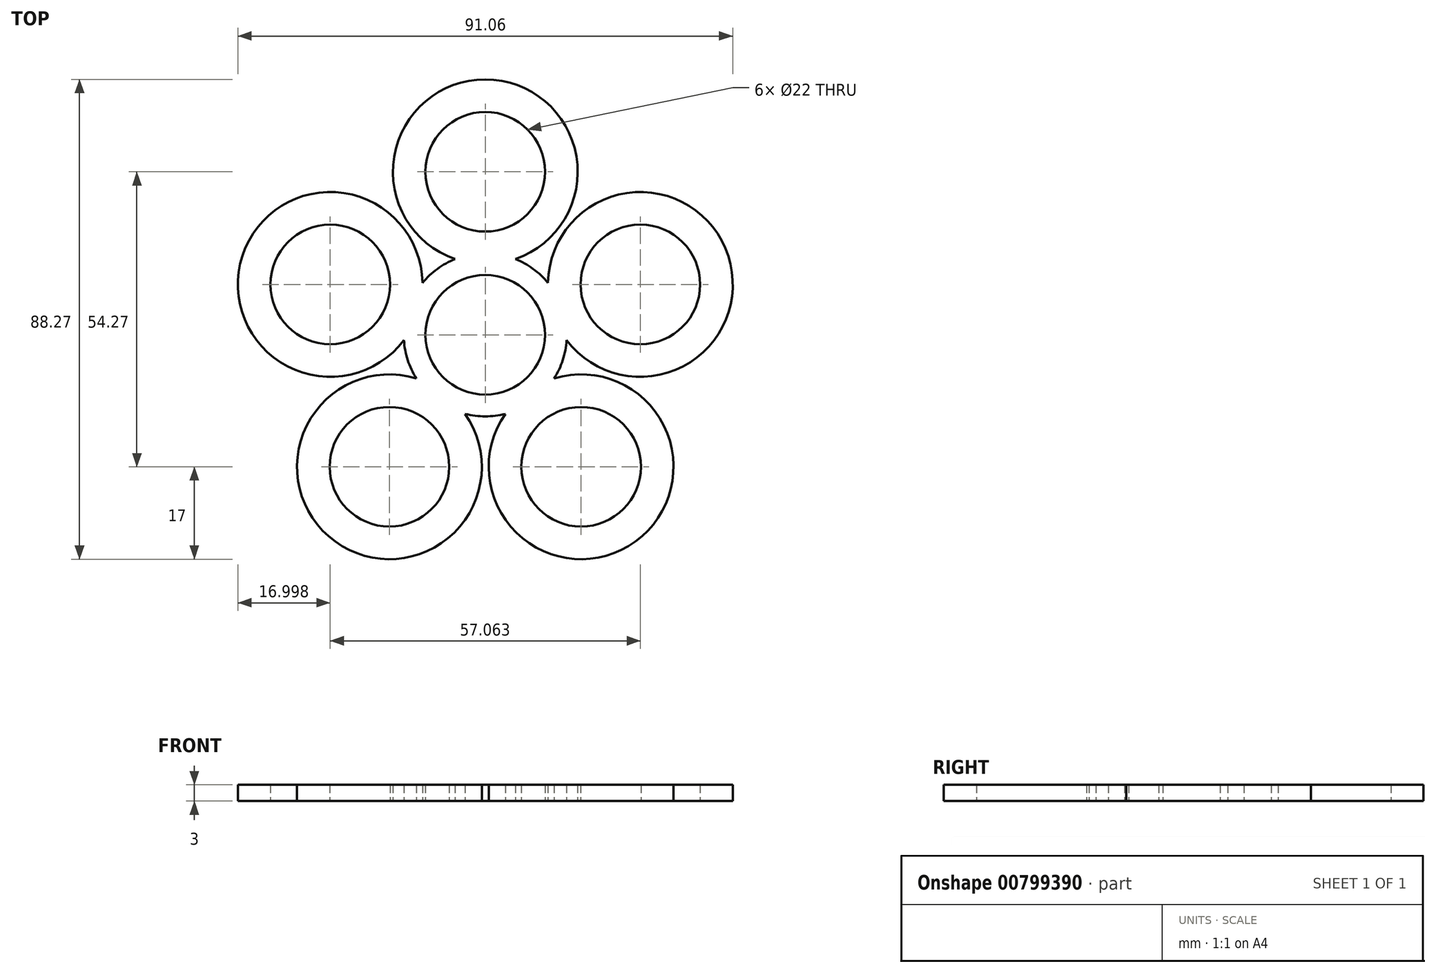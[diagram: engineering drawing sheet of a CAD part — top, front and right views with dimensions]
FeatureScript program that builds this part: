
annotation { "Feature Type Name" : "Feature", "Feature Type Description" : "" }
export const myFeature = defineFeature(function(context is Context, id is Id, definition is map)
    precondition{}
    {
        {
            var Q0;
            Q0=qCreatedBy(makeId("Top.planeOp"),FACE);
            var sketch = newSketch(context, id + "F0", { "sketchPlane" : qUnion([Q0])});
            skCircle(sketch, "E0", {"center": v(0, 0) * mm, "radius": 11 * mm});
            skArc(sketch, "E1", {"start": v(-3.7, -14.54) * mm, "mid": v(0, -15) * mm, "end": v(3.7, -14.54) * mm});
            skCircle(sketch, "E2", {"center": v(0, 30) * mm, "radius": 11 * mm});
            skArc(sketch, "E3", {"start": v(5.56, 13.93) * mm, "mid": v(0, 47) * mm, "end": v(-5.56, 13.93) * mm});
            skLineSegment(sketch, "E4", {"start": v(27.63, -38.02) * mm, "end": v(29.53, -40.65) * mm});
            skArc(sketch, "E5.1.0", {"start": v(-11.53, 9.59) * mm, "mid": v(-44.7, 14.52) * mm, "end": v(-14.97, -0.98) * mm});
            skCircle(sketch, "E5.1.1", {"center": v(-28.53, 9.27) * mm, "radius": 11 * mm});
            skArc(sketch, "E5.2.0", {"start": v(-12.68, -8) * mm, "mid": v(-27.63, -38.02) * mm, "end": v(-3.7, -14.54) * mm});
            skCircle(sketch, "E5.2.1", {"center": v(-17.63, -24.27) * mm, "radius": 11 * mm});
            skArc(sketch, "E5.3.0", {"start": v(3.7, -14.54) * mm, "mid": v(27.63, -38.02) * mm, "end": v(12.68, -8) * mm});
            skCircle(sketch, "E5.3.1", {"center": v(17.63, -24.27) * mm, "radius": 11 * mm});
            skArc(sketch, "E5.4.0", {"start": v(14.97, -0.98) * mm, "mid": v(44.7, 14.52) * mm, "end": v(11.53, 9.59) * mm});
            skCircle(sketch, "E5.4.1", {"center": v(28.53, 9.27) * mm, "radius": 11 * mm});
            skLineSegment(sketch, "E6.trimOffspring", {"start": v(-27.63, -38.02) * mm, "end": v(-28.31, -38.97) * mm});
            skArc(sketch, "E7.trimOffspring", {"start": v(-14.97, -0.98) * mm, "mid": v(-14.27, -4.64) * mm, "end": v(-12.68, -8) * mm});
            skArc(sketch, "E8.trimOffspring", {"start": v(-5.56, 13.93) * mm, "mid": v(-8.82, 12.14) * mm, "end": v(-11.53, 9.59) * mm});
            skArc(sketch, "E9.trimOffspring", {"start": v(12.68, -8) * mm, "mid": v(14.27, -4.64) * mm, "end": v(14.97, -0.98) * mm});
            skArc(sketch, "E10.trimOffspring", {"start": v(11.53, 9.59) * mm, "mid": v(8.82, 12.14) * mm, "end": v(5.56, 13.93) * mm});
            skSolve(sketch);
        }
        {
            var Q0;
            Q0 = qSketchRegion(id + "F0", true);
            extrude(context, id + "F1", {"entities" : qUnion([Q0]), "depth" : 3 * mm, "offsetDistance" : 25 * mm});
        }
    });
